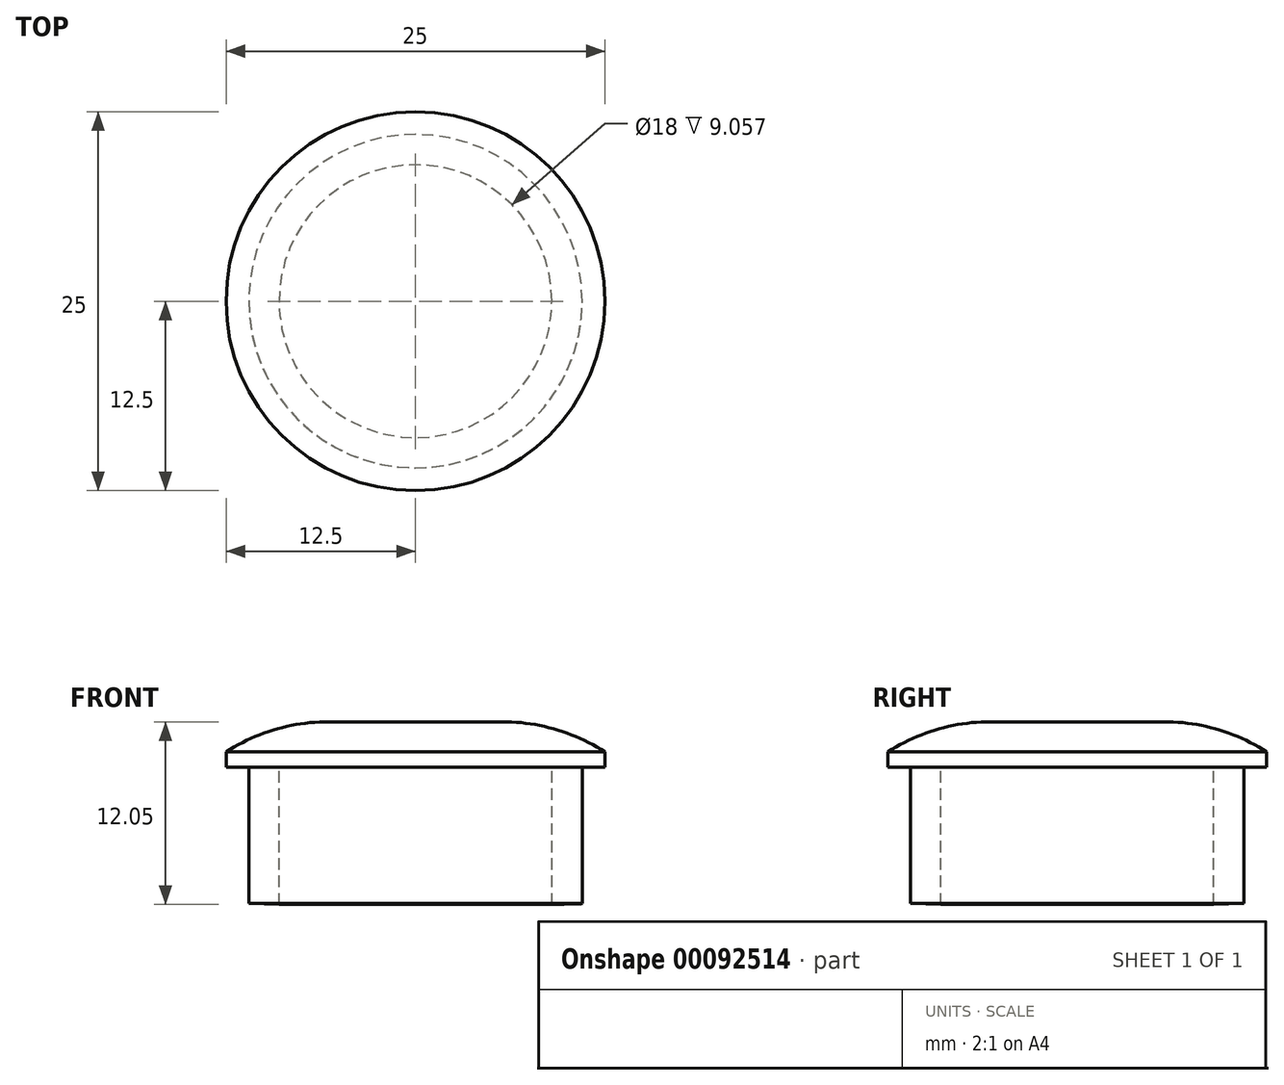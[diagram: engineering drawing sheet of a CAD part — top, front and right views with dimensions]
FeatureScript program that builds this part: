
annotation { "Feature Type Name" : "Feature", "Feature Type Description" : "" }
export const myFeature = defineFeature(function(context is Context, id is Id, definition is map)
    precondition{}
    {
        {
            var Q0;
            Q0=qCreatedBy(makeId("Front.planeOp"),FACE);
            var sketch = newSketch(context, id + "F0", { "sketchPlane" : qUnion([Q0])});
            skLineSegment(sketch, "E0", {"start": v(0, 10.2) * mm, "end": v(-12.5, 10.2) * mm});
            skLineSegment(sketch, "E1", {"start": v(-12.5, 10.2) * mm, "end": v(-12.5, 8.2) * mm});
            skLineSegment(sketch, "E2", {"start": v(-12.5, 8.2) * mm, "end": v(-11, 8.2) * mm});
            skLineSegment(sketch, "E3", {"start": v(-11, 8.2) * mm, "end": v(-11, -1.8) * mm});
            skLineSegment(sketch, "E4", {"start": v(0, 10.2) * mm, "end": v(0, 7.2) * mm});
            skLineSegment(sketch, "E5", {"start": v(0, 7.2) * mm, "end": v(-9, 7.2) * mm});
            skLineSegment(sketch, "E6", {"start": v(-9, 7.2) * mm, "end": v(-9, -1.85) * mm});
            skLineSegment(sketch, "E7", {"start": v(-9, -1.85) * mm, "end": v(-11, -1.8) * mm});
            skSolve(sketch);
        }
        {
            var Q0;
            Q0=makeQuery(id+"F0.imprint","IMPRINT",FACE,{"disambiguationData":[TD([[makeQuery(id+"F0.imprint","IMPRINT",EDGE,{"derivedFrom":sQuery(id+"F0.wireOp",EDGE,"E0")}),1.0]])]});
            var Q1;
            Q1=sQuery(id+"F0.wireOp",EDGE,"E4");
            revolve(context, id + "F1", {"entities" : qUnion([Q0]), "axis" : qUnion([Q1]), "revolveType" : RevolveType.FULL});
        }
        {
            var Q0;
            Q0=makeQuery(id+"F1.opRevolve","SWEPT_FACE",FACE,{"disambiguationData":[OSD([sQuery(id+"F0.wireOp",EDGE,"E0")])]});
            fillet(context, id + "F2", {"entities" : qUnion([Q0]), "radius" : 12.5 * mm, "tangentPropagation" : true, "allowEdgeOverflow" : false});
        }
        {
            var Q0;
            Q0=makeQuery(id+"F1.opRevolve","SWEPT_FACE",FACE,{"disambiguationData":[OSD([sQuery(id+"F0.wireOp",EDGE,"E2")])]});
            extrude(context, id + "F3", {"entities" : qUnion([Q0]), "operationType" : NewBodyOperationType.ADD, "depth" : 1 * mm});
        }
    });
